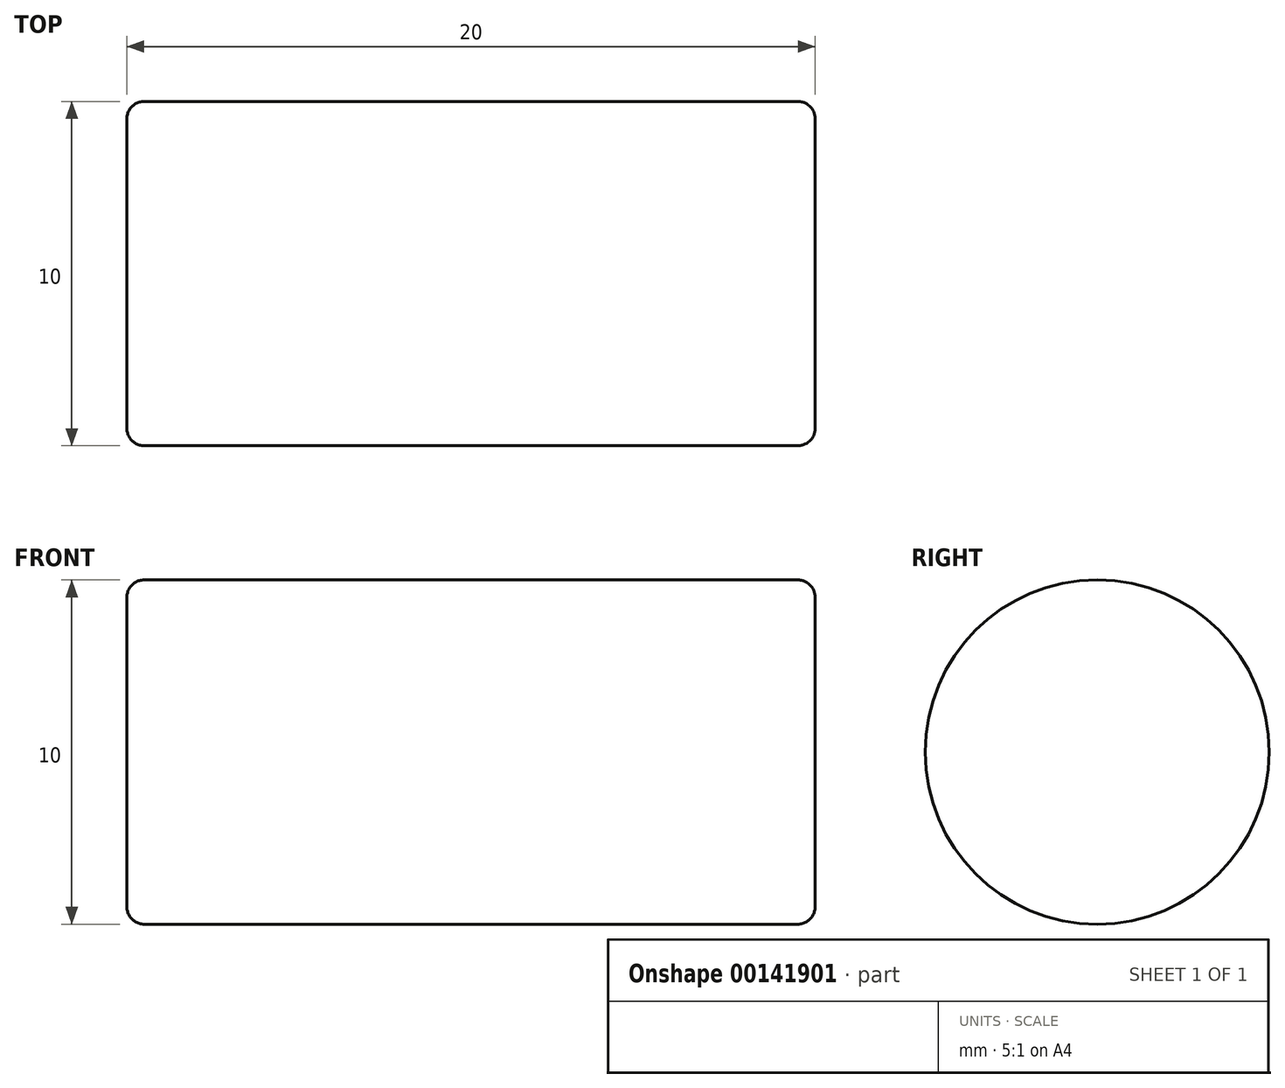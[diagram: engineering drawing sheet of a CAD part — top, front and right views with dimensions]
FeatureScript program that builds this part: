
annotation { "Feature Type Name" : "Feature", "Feature Type Description" : "" }
export const myFeature = defineFeature(function(context is Context, id is Id, definition is map)
    precondition{}
    {
        {
            var Q0;
            Q0=qCreatedBy(makeId("Right.planeOp"),FACE);
            var sketch = newSketch(context, id + "F0", { "sketchPlane" : qUnion([Q0])});
            skCircle(sketch, "E0", {"center": v(0, 0) * mm, "radius": 5 * mm});
            skSolve(sketch);
        }
        {
            var Q0;
            Q0 = qSketchRegion(id + "F0", true);
            var Q1;
            Q1=makeQuery(id+"F0.imprint","IMPRINT",FACE,{"disambiguationData":[TD([[makeQuery(id+"F0.imprint","IMPRINT",EDGE,{"derivedFrom":sQuery(id+"F0.wireOp",EDGE,"E0")}),1.0]])]});
            extrude(context, id + "F1", {"entities" : qUnion([Q0, Q1]), "depth" : 20 * mm});
        }
        {
            var Q0;
            Q0=makeQuery(id+"F1.opExtrude","CAP_FACE",FACE,{"disambiguationData":[OSD([sQuery(id+"F0.wireOp",EDGE,"E0")])],"isStart":false});
            var Q1;
            Q1=makeQuery(id+"F1.opExtrude","CAP_FACE",FACE,{"disambiguationData":[OSD([sQuery(id+"F0.wireOp",EDGE,"E0")])],"isStart":true});
            fillet(context, id + "F2", {"entities" : qUnion([Q0, Q1]), "radius" : 0.5 * mm, "tangentPropagation" : true, "allowEdgeOverflow" : false});
        }
    });
